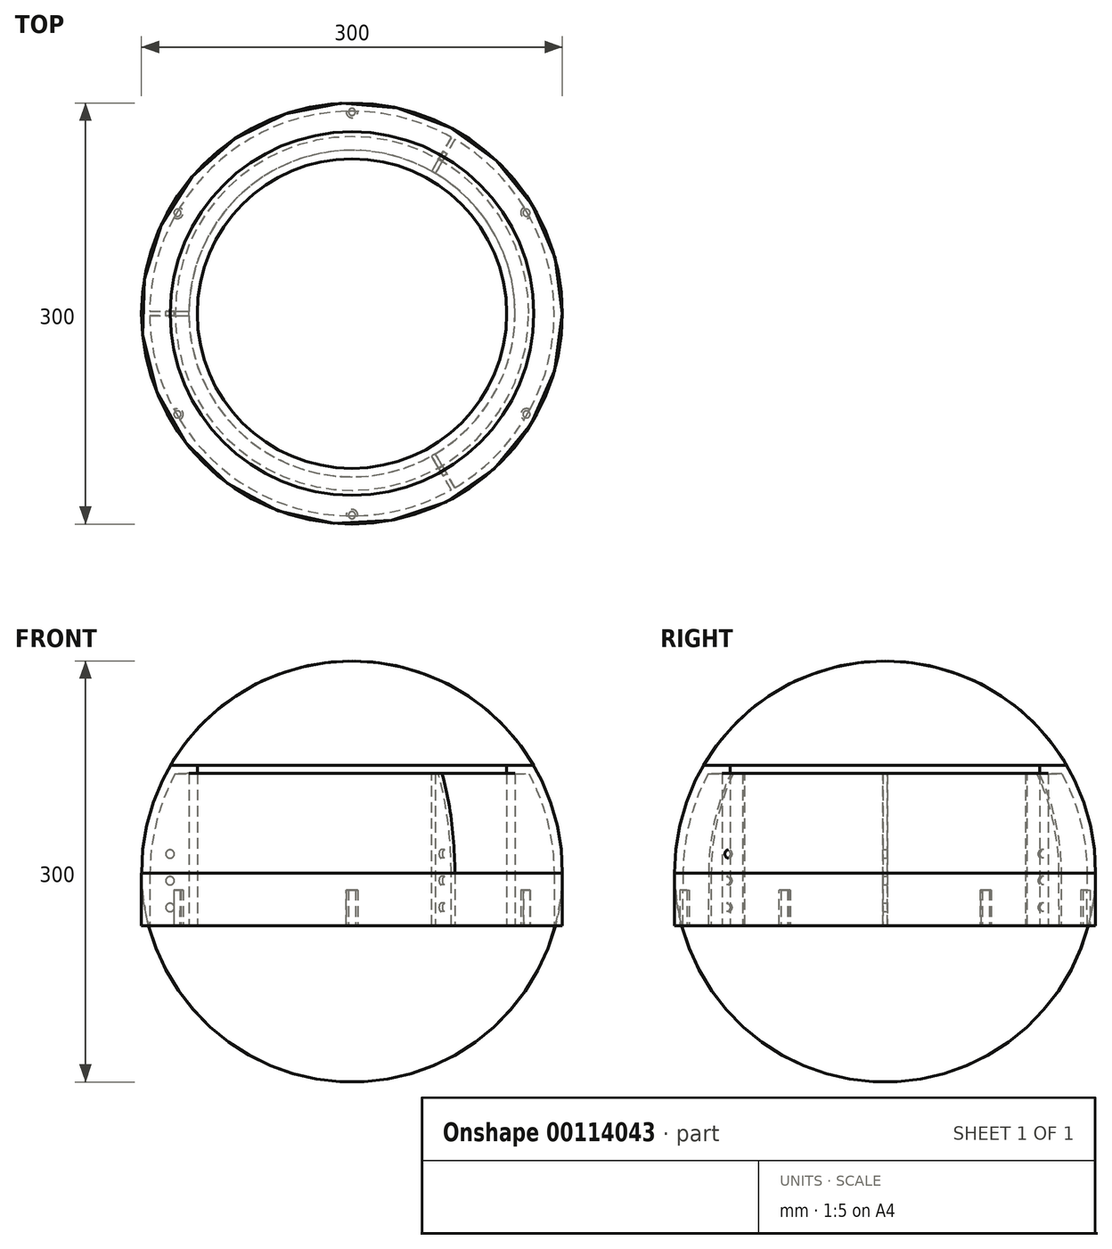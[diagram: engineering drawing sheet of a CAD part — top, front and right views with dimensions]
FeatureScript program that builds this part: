
annotation { "Feature Type Name" : "Feature", "Feature Type Description" : "" }
export const myFeature = defineFeature(function(context is Context, id is Id, definition is map)
    precondition{}
    {
        {
            var Q0;
            Q0=qCreatedBy(makeId("Front.planeOp"),FACE);
            var sketch = newSketch(context, id + "F0", { "sketchPlane" : qUnion([Q0])});
            skArc(sketch, "E0.trimOffspring", {"start": v(-125.97, 71) * mm, "mid": v(-139.35, 36.6) * mm, "end": v(-144, 0) * mm});
            skLineSegment(sketch, "E1", {"start": v(-116.3, 71.03) * mm, "end": v(-116.3, -24.99) * mm});
            skLineSegment(sketch, "E2", {"start": v(-150, 0) * mm, "end": v(-150, -37.33) * mm});
            skLineSegment(sketch, "E3", {"start": v(-150, -37.33) * mm, "end": v(-116.3, -37.33) * mm});
            skLineSegment(sketch, "E4", {"start": v(-116.3, -37.33) * mm, "end": v(-116.3, -24.99) * mm});
            skLineSegment(sketch, "E5", {"start": v(-144, 0) * mm, "end": v(-144.14, -37.33) * mm});
            skArc(sketch, "E6.trimOffspring", {"start": v(-129.51, 76.97) * mm, "mid": v(-144.96, 39.87) * mm, "end": v(-150, 0) * mm});
            skLineSegment(sketch, "E7", {"start": v(-129.51, 76.97) * mm, "end": v(-116.3, 76.97) * mm});
            skLineSegment(sketch, "E8", {"start": v(-116.3, 71.03) * mm, "end": v(-125.97, 71) * mm});
            skLineSegment(sketch, "E9", {"start": v(-125.99, 70.97) * mm, "end": v(-116.3, 70.97) * mm});
            skLineSegment(sketch, "E10", {"start": v(-110.3, 70.97) * mm, "end": v(-110.3, -37.33) * mm});
            skLineSegment(sketch, "E11", {"start": v(-110.3, -37.33) * mm, "end": v(-116.3, -37.33) * mm});
            skLineSegment(sketch, "E12", {"start": v(-116.3, 76.97) * mm, "end": v(-110.3, 76.97) * mm});
            skLineSegment(sketch, "E13", {"start": v(-110.3, 76.97) * mm, "end": v(-110.3, 70.97) * mm});
            skLineSegment(sketch, "E14", {"start": v(0, -70.43) * mm, "end": v(0, 79.54) * mm, "construction": true});
            skSolve(sketch);
        }
        {
            var Q0;
            {var subQ6=sQuery(id+"F0.wireOp",EDGE,"E2");Q0=makeQuery(id+"F0.imprint","IMPRINT",FACE,{"disambiguationData":[TD([[makeQuery(id+"F0.imprint","IMPRINT",EDGE,{"derivedFrom":subQ6}),1.0]])]});}
            var Q1;
            Q1=sQuery(id+"F0.wireOp",EDGE,"E14");
            revolve(context, id + "F1", {"entities" : qUnion([Q0]), "axis" : qUnion([Q1]), "revolveType" : RevolveType.FULL});
        }
        {
            var Q0;
            Q0=makeQuery(id+"F1.opRevolve","SWEPT_FACE",FACE,{"disambiguationData":[OSD([sQuery(id+"F0.wireOp",EDGE,"E3")])]});
            var sketch = newSketch(context, id + "F2", { "sketchPlane" : qUnion([Q0])});
            skCircle(sketch, "E15", {"center": v(0, 143.67) * mm, "radius": 2.5 * mm});
            skCircle(sketch, "E16", {"center": v(0, 143.67) * mm, "radius": 4.13 * mm});
            skCircle(sketch, "E17.1.0", {"center": v(-124.42, 71.83) * mm, "radius": 2.5 * mm});
            skCircle(sketch, "E17.2.0", {"center": v(-124.42, -71.83) * mm, "radius": 2.5 * mm});
            skCircle(sketch, "E17.3.0", {"center": v(0, -143.67) * mm, "radius": 2.5 * mm});
            skCircle(sketch, "E17.4.0", {"center": v(124.42, -71.83) * mm, "radius": 2.5 * mm});
            skCircle(sketch, "E17.5.0", {"center": v(124.42, 71.83) * mm, "radius": 2.5 * mm});
            skPoint(sketch, "E17.center", {"position": v(0, 0) * mm});
            skCircle(sketch, "E18.1.0", {"center": v(-124.42, -71.83) * mm, "radius": 4.13 * mm});
            skCircle(sketch, "E18.2.0", {"center": v(124.42, -71.83) * mm, "radius": 4.13 * mm});
            skCircle(sketch, "E19.1.0", {"center": v(-124.42, 71.83) * mm, "radius": 4.13 * mm});
            skCircle(sketch, "E19.3.0", {"center": v(0, -143.67) * mm, "radius": 4.13 * mm});
            skCircle(sketch, "E19.5.0", {"center": v(124.42, 71.83) * mm, "radius": 4.13 * mm});
            skSolve(sketch);
        }
        {
            var Q0;
            {var subQ0=sQuery(id+"F2.wireOp",EDGE,"E17.4.0");var subQ1=makeQuery(id+"F1.opRevolve","SWEPT_EDGE",EDGE,{"disambiguationData":[OSD([sQuery(id+"F0.wireOp",EDGE,"E3"),sQuery(id+"F0.wireOp",EDGE,"E5")])]});var subQ2=makeQuery(id+"F2.imprint","INTERSECT",VERTEX,{"disambiguationData":[OD(0.0)],"derivedFrom":[subQ1,subQ0]});Q0=makeQuery(id+"F2.imprint","IMPRINT",FACE,{"disambiguationData":[TD([[makeQuery(id+"F2.imprint","IMPRINT",EDGE,{"disambiguationData":[TD([[subQ2,-1.0]])],"derivedFrom":subQ0}),1.0]])]});}
            var Q1;
            {var subQ0=sQuery(id+"F2.wireOp",EDGE,"E15");var subQ1=makeQuery(id+"F1.opRevolve","SWEPT_EDGE",EDGE,{"disambiguationData":[OSD([sQuery(id+"F0.wireOp",EDGE,"E3"),sQuery(id+"F0.wireOp",EDGE,"E5")])]});var subQ2=makeQuery(id+"F2.imprint","INTERSECT",VERTEX,{"disambiguationData":[OD(0.0)],"derivedFrom":[subQ1,subQ0]});Q1=makeQuery(id+"F2.imprint","IMPRINT",FACE,{"disambiguationData":[TD([[makeQuery(id+"F2.imprint","IMPRINT",EDGE,{"disambiguationData":[TD([[subQ2,1.0]])],"derivedFrom":subQ0}),-1.0]])]});}
            var Q2;
            {var subQ0=sQuery(id+"F2.wireOp",EDGE,"E15");var subQ1=makeQuery(id+"F1.opRevolve","SWEPT_EDGE",EDGE,{"disambiguationData":[OSD([sQuery(id+"F0.wireOp",EDGE,"E3"),sQuery(id+"F0.wireOp",EDGE,"E5")])]});var subQ2=makeQuery(id+"F2.imprint","INTERSECT",VERTEX,{"disambiguationData":[OD(0.0)],"derivedFrom":[subQ1,subQ0]});Q2=makeQuery(id+"F2.imprint","IMPRINT",FACE,{"disambiguationData":[TD([[makeQuery(id+"F2.imprint","IMPRINT",EDGE,{"disambiguationData":[TD([[subQ2,-1.0]])],"derivedFrom":subQ0}),-1.0]])]});}
            var Q3;
            {var subQ0=sQuery(id+"F2.wireOp",EDGE,"E17.1.0");var subQ1=makeQuery(id+"F1.opRevolve","SWEPT_EDGE",EDGE,{"disambiguationData":[OSD([sQuery(id+"F0.wireOp",EDGE,"E3"),sQuery(id+"F0.wireOp",EDGE,"E5")])]});var subQ2=makeQuery(id+"F2.imprint","INTERSECT",VERTEX,{"disambiguationData":[OD(0.0)],"derivedFrom":[subQ1,subQ0]});Q3=makeQuery(id+"F2.imprint","IMPRINT",FACE,{"disambiguationData":[TD([[makeQuery(id+"F2.imprint","IMPRINT",EDGE,{"disambiguationData":[TD([[subQ2,-1.0]])],"derivedFrom":subQ0}),-1.0]])]});}
            var Q4;
            {var subQ0=sQuery(id+"F2.wireOp",EDGE,"E17.1.0");var subQ1=makeQuery(id+"F1.opRevolve","SWEPT_EDGE",EDGE,{"disambiguationData":[OSD([sQuery(id+"F0.wireOp",EDGE,"E3"),sQuery(id+"F0.wireOp",EDGE,"E5")])]});var subQ2=makeQuery(id+"F2.imprint","INTERSECT",VERTEX,{"disambiguationData":[OD(0.0)],"derivedFrom":[subQ1,subQ0]});Q4=makeQuery(id+"F2.imprint","IMPRINT",FACE,{"disambiguationData":[TD([[makeQuery(id+"F2.imprint","IMPRINT",EDGE,{"disambiguationData":[TD([[subQ2,1.0]])],"derivedFrom":subQ0}),-1.0]])]});}
            var Q5;
            {var subQ0=sQuery(id+"F2.wireOp",EDGE,"E17.5.0");var subQ1=makeQuery(id+"F1.opRevolve","SWEPT_EDGE",EDGE,{"disambiguationData":[OSD([sQuery(id+"F0.wireOp",EDGE,"E3"),sQuery(id+"F0.wireOp",EDGE,"E5")])]});var subQ2=makeQuery(id+"F2.imprint","INTERSECT",VERTEX,{"disambiguationData":[OD(0.0)],"derivedFrom":[subQ1,subQ0]});Q5=makeQuery(id+"F2.imprint","IMPRINT",FACE,{"disambiguationData":[TD([[makeQuery(id+"F2.imprint","IMPRINT",EDGE,{"disambiguationData":[TD([[subQ2,-1.0]])],"derivedFrom":subQ0}),-1.0]])]});}
            var Q6;
            {var subQ0=sQuery(id+"F2.wireOp",EDGE,"E17.5.0");var subQ1=makeQuery(id+"F1.opRevolve","SWEPT_EDGE",EDGE,{"disambiguationData":[OSD([sQuery(id+"F0.wireOp",EDGE,"E3"),sQuery(id+"F0.wireOp",EDGE,"E5")])]});var subQ2=makeQuery(id+"F2.imprint","INTERSECT",VERTEX,{"disambiguationData":[OD(0.0)],"derivedFrom":[subQ1,subQ0]});Q6=makeQuery(id+"F2.imprint","IMPRINT",FACE,{"disambiguationData":[TD([[makeQuery(id+"F2.imprint","IMPRINT",EDGE,{"disambiguationData":[TD([[subQ2,1.0]])],"derivedFrom":subQ0}),-1.0]])]});}
            var Q7;
            {var subQ0=sQuery(id+"F2.wireOp",EDGE,"E17.2.0");var subQ1=makeQuery(id+"F1.opRevolve","SWEPT_EDGE",EDGE,{"disambiguationData":[OSD([sQuery(id+"F0.wireOp",EDGE,"E3"),sQuery(id+"F0.wireOp",EDGE,"E5")])]});var subQ2=makeQuery(id+"F2.imprint","INTERSECT",VERTEX,{"disambiguationData":[OD(0.0)],"derivedFrom":[subQ1,subQ0]});Q7=makeQuery(id+"F2.imprint","IMPRINT",FACE,{"disambiguationData":[TD([[makeQuery(id+"F2.imprint","IMPRINT",EDGE,{"disambiguationData":[TD([[subQ2,-1.0]])],"derivedFrom":subQ0}),-1.0]])]});}
            var Q8;
            {var subQ0=sQuery(id+"F2.wireOp",EDGE,"E17.2.0");var subQ1=makeQuery(id+"F1.opRevolve","SWEPT_EDGE",EDGE,{"disambiguationData":[OSD([sQuery(id+"F0.wireOp",EDGE,"E3"),sQuery(id+"F0.wireOp",EDGE,"E5")])]});var subQ2=makeQuery(id+"F2.imprint","INTERSECT",VERTEX,{"disambiguationData":[OD(0.0)],"derivedFrom":[subQ1,subQ0]});Q8=makeQuery(id+"F2.imprint","IMPRINT",FACE,{"disambiguationData":[TD([[makeQuery(id+"F2.imprint","IMPRINT",EDGE,{"disambiguationData":[TD([[subQ2,1.0]])],"derivedFrom":subQ0}),-1.0]])]});}
            var Q9;
            {var subQ0=sQuery(id+"F2.wireOp",EDGE,"E17.2.0");var subQ1=makeQuery(id+"F1.opRevolve","SWEPT_EDGE",EDGE,{"disambiguationData":[OSD([sQuery(id+"F0.wireOp",EDGE,"E3"),sQuery(id+"F0.wireOp",EDGE,"E5")])]});var subQ2=makeQuery(id+"F2.imprint","INTERSECT",VERTEX,{"disambiguationData":[OD(0.0)],"derivedFrom":[subQ1,subQ0]});Q9=makeQuery(id+"F2.imprint","IMPRINT",FACE,{"disambiguationData":[TD([[makeQuery(id+"F2.imprint","IMPRINT",EDGE,{"disambiguationData":[TD([[subQ2,-1.0]])],"derivedFrom":subQ0}),1.0]])]});}
            var Q10;
            {var subQ0=sQuery(id+"F2.wireOp",EDGE,"E17.4.0");var subQ1=makeQuery(id+"F1.opRevolve","SWEPT_EDGE",EDGE,{"disambiguationData":[OSD([sQuery(id+"F0.wireOp",EDGE,"E3"),sQuery(id+"F0.wireOp",EDGE,"E5")])]});var subQ2=makeQuery(id+"F2.imprint","INTERSECT",VERTEX,{"disambiguationData":[OD(0.0)],"derivedFrom":[subQ1,subQ0]});Q10=makeQuery(id+"F2.imprint","IMPRINT",FACE,{"disambiguationData":[TD([[makeQuery(id+"F2.imprint","IMPRINT",EDGE,{"disambiguationData":[TD([[subQ2,-1.0]])],"derivedFrom":subQ0}),-1.0]])]});}
            var Q11;
            {var subQ0=sQuery(id+"F2.wireOp",EDGE,"E17.4.0");var subQ1=makeQuery(id+"F1.opRevolve","SWEPT_EDGE",EDGE,{"disambiguationData":[OSD([sQuery(id+"F0.wireOp",EDGE,"E3"),sQuery(id+"F0.wireOp",EDGE,"E5")])]});var subQ2=makeQuery(id+"F2.imprint","INTERSECT",VERTEX,{"disambiguationData":[OD(0.0)],"derivedFrom":[subQ1,subQ0]});Q11=makeQuery(id+"F2.imprint","IMPRINT",FACE,{"disambiguationData":[TD([[makeQuery(id+"F2.imprint","IMPRINT",EDGE,{"disambiguationData":[TD([[subQ2,1.0]])],"derivedFrom":subQ0}),-1.0]])]});}
            var Q12;
            {var subQ0=sQuery(id+"F2.wireOp",EDGE,"E17.3.0");var subQ1=makeQuery(id+"F1.opRevolve","SWEPT_EDGE",EDGE,{"disambiguationData":[OSD([sQuery(id+"F0.wireOp",EDGE,"E3"),sQuery(id+"F0.wireOp",EDGE,"E5")])]});var subQ2=makeQuery(id+"F2.imprint","INTERSECT",VERTEX,{"disambiguationData":[OD(0.0)],"derivedFrom":[subQ1,subQ0]});Q12=makeQuery(id+"F2.imprint","IMPRINT",FACE,{"disambiguationData":[TD([[makeQuery(id+"F2.imprint","IMPRINT",EDGE,{"disambiguationData":[TD([[subQ2,1.0]])],"derivedFrom":subQ0}),-1.0]])]});}
            extrude(context, id + "F3", {"entities" : qUnion([Q0, Q1, Q2, Q3, Q4, Q5, Q6, Q7, Q8, Q9, Q10, Q11, Q12]), "operationType" : NewBodyOperationType.ADD, "oppositeDirection" : true, "depth" : 25.4 * mm});
        }
        {
            var Q0;
            {var subQ0=sQuery(id+"F2.wireOp",EDGE,"E17.1.0");var subQ1=makeQuery(id+"F1.opRevolve","SWEPT_EDGE",EDGE,{"disambiguationData":[OSD([sQuery(id+"F0.wireOp",EDGE,"E3"),sQuery(id+"F0.wireOp",EDGE,"E5")])]});var subQ2=makeQuery(id+"F2.imprint","INTERSECT",VERTEX,{"disambiguationData":[OD(0.0)],"derivedFrom":[subQ1,subQ0]});Q0=makeQuery(id+"F2.imprint","IMPRINT",FACE,{"disambiguationData":[TD([[makeQuery(id+"F2.imprint","IMPRINT",EDGE,{"disambiguationData":[TD([[subQ2,1.0]])],"derivedFrom":subQ0}),1.0]])]});}
            var Q1;
            {var subQ0=sQuery(id+"F2.wireOp",EDGE,"E17.1.0");var subQ1=makeQuery(id+"F1.opRevolve","SWEPT_EDGE",EDGE,{"disambiguationData":[OSD([sQuery(id+"F0.wireOp",EDGE,"E3"),sQuery(id+"F0.wireOp",EDGE,"E5")])]});var subQ2=makeQuery(id+"F2.imprint","INTERSECT",VERTEX,{"disambiguationData":[OD(0.0)],"derivedFrom":[subQ1,subQ0]});Q1=makeQuery(id+"F2.imprint","IMPRINT",FACE,{"disambiguationData":[TD([[makeQuery(id+"F2.imprint","IMPRINT",EDGE,{"disambiguationData":[TD([[subQ2,-1.0]])],"derivedFrom":subQ0}),1.0]])]});}
            var Q2;
            {var subQ0=sQuery(id+"F2.wireOp",EDGE,"E15");var subQ1=makeQuery(id+"F1.opRevolve","SWEPT_EDGE",EDGE,{"disambiguationData":[OSD([sQuery(id+"F0.wireOp",EDGE,"E3"),sQuery(id+"F0.wireOp",EDGE,"E5")])]});var subQ2=makeQuery(id+"F2.imprint","INTERSECT",VERTEX,{"disambiguationData":[OD(0.0)],"derivedFrom":[subQ1,subQ0]});Q2=makeQuery(id+"F2.imprint","IMPRINT",FACE,{"disambiguationData":[TD([[makeQuery(id+"F2.imprint","IMPRINT",EDGE,{"disambiguationData":[TD([[subQ2,1.0]])],"derivedFrom":subQ0}),1.0]])]});}
            var Q3;
            {var subQ0=sQuery(id+"F2.wireOp",EDGE,"E15");var subQ1=makeQuery(id+"F1.opRevolve","SWEPT_EDGE",EDGE,{"disambiguationData":[OSD([sQuery(id+"F0.wireOp",EDGE,"E3"),sQuery(id+"F0.wireOp",EDGE,"E5")])]});var subQ2=makeQuery(id+"F2.imprint","INTERSECT",VERTEX,{"disambiguationData":[OD(0.0)],"derivedFrom":[subQ1,subQ0]});Q3=makeQuery(id+"F2.imprint","IMPRINT",FACE,{"disambiguationData":[TD([[makeQuery(id+"F2.imprint","IMPRINT",EDGE,{"disambiguationData":[TD([[subQ2,-1.0]])],"derivedFrom":subQ0}),1.0]])]});}
            var Q4;
            {var subQ0=sQuery(id+"F2.wireOp",EDGE,"E17.5.0");var subQ1=makeQuery(id+"F1.opRevolve","SWEPT_EDGE",EDGE,{"disambiguationData":[OSD([sQuery(id+"F0.wireOp",EDGE,"E3"),sQuery(id+"F0.wireOp",EDGE,"E5")])]});var subQ2=makeQuery(id+"F2.imprint","INTERSECT",VERTEX,{"disambiguationData":[OD(0.0)],"derivedFrom":[subQ1,subQ0]});Q4=makeQuery(id+"F2.imprint","IMPRINT",FACE,{"disambiguationData":[TD([[makeQuery(id+"F2.imprint","IMPRINT",EDGE,{"disambiguationData":[TD([[subQ2,1.0]])],"derivedFrom":subQ0}),1.0]])]});}
            var Q5;
            {var subQ0=sQuery(id+"F2.wireOp",EDGE,"E17.5.0");var subQ1=makeQuery(id+"F1.opRevolve","SWEPT_EDGE",EDGE,{"disambiguationData":[OSD([sQuery(id+"F0.wireOp",EDGE,"E3"),sQuery(id+"F0.wireOp",EDGE,"E5")])]});var subQ2=makeQuery(id+"F2.imprint","INTERSECT",VERTEX,{"disambiguationData":[OD(0.0)],"derivedFrom":[subQ1,subQ0]});Q5=makeQuery(id+"F2.imprint","IMPRINT",FACE,{"disambiguationData":[TD([[makeQuery(id+"F2.imprint","IMPRINT",EDGE,{"disambiguationData":[TD([[subQ2,-1.0]])],"derivedFrom":subQ0}),1.0]])]});}
            var Q6;
            {var subQ0=sQuery(id+"F2.wireOp",EDGE,"E17.2.0");var subQ1=makeQuery(id+"F1.opRevolve","SWEPT_EDGE",EDGE,{"disambiguationData":[OSD([sQuery(id+"F0.wireOp",EDGE,"E3"),sQuery(id+"F0.wireOp",EDGE,"E5")])]});var subQ2=makeQuery(id+"F2.imprint","INTERSECT",VERTEX,{"disambiguationData":[OD(0.0)],"derivedFrom":[subQ1,subQ0]});Q6=makeQuery(id+"F2.imprint","IMPRINT",FACE,{"disambiguationData":[TD([[makeQuery(id+"F2.imprint","IMPRINT",EDGE,{"disambiguationData":[TD([[subQ2,-1.0]])],"derivedFrom":subQ0}),1.0]])]});}
            var Q7;
            {var subQ0=sQuery(id+"F2.wireOp",EDGE,"E17.2.0");var subQ1=makeQuery(id+"F1.opRevolve","SWEPT_EDGE",EDGE,{"disambiguationData":[OSD([sQuery(id+"F0.wireOp",EDGE,"E3"),sQuery(id+"F0.wireOp",EDGE,"E5")])]});var subQ2=makeQuery(id+"F2.imprint","INTERSECT",VERTEX,{"disambiguationData":[OD(0.0)],"derivedFrom":[subQ1,subQ0]});Q7=makeQuery(id+"F2.imprint","IMPRINT",FACE,{"disambiguationData":[TD([[makeQuery(id+"F2.imprint","IMPRINT",EDGE,{"disambiguationData":[TD([[subQ2,1.0]])],"derivedFrom":subQ0}),1.0]])]});}
            var Q8;
            {var subQ0=sQuery(id+"F2.wireOp",EDGE,"E17.3.0");var subQ1=makeQuery(id+"F1.opRevolve","SWEPT_EDGE",EDGE,{"disambiguationData":[OSD([sQuery(id+"F0.wireOp",EDGE,"E3"),sQuery(id+"F0.wireOp",EDGE,"E5")])]});var subQ2=makeQuery(id+"F2.imprint","INTERSECT",VERTEX,{"disambiguationData":[OD(0.0)],"derivedFrom":[subQ1,subQ0]});Q8=makeQuery(id+"F2.imprint","IMPRINT",FACE,{"disambiguationData":[TD([[makeQuery(id+"F2.imprint","IMPRINT",EDGE,{"disambiguationData":[TD([[subQ2,-1.0]])],"derivedFrom":subQ0}),1.0]])]});}
            var Q9;
            {var subQ0=sQuery(id+"F2.wireOp",EDGE,"E17.3.0");var subQ1=makeQuery(id+"F1.opRevolve","SWEPT_EDGE",EDGE,{"disambiguationData":[OSD([sQuery(id+"F0.wireOp",EDGE,"E3"),sQuery(id+"F0.wireOp",EDGE,"E5")])]});var subQ2=makeQuery(id+"F2.imprint","INTERSECT",VERTEX,{"disambiguationData":[OD(0.0)],"derivedFrom":[subQ1,subQ0]});Q9=makeQuery(id+"F2.imprint","IMPRINT",FACE,{"disambiguationData":[TD([[makeQuery(id+"F2.imprint","IMPRINT",EDGE,{"disambiguationData":[TD([[subQ2,1.0]])],"derivedFrom":subQ0}),1.0]])]});}
            var Q10;
            {var subQ0=sQuery(id+"F2.wireOp",EDGE,"E17.4.0");var subQ1=makeQuery(id+"F1.opRevolve","SWEPT_EDGE",EDGE,{"disambiguationData":[OSD([sQuery(id+"F0.wireOp",EDGE,"E3"),sQuery(id+"F0.wireOp",EDGE,"E5")])]});var subQ2=makeQuery(id+"F2.imprint","INTERSECT",VERTEX,{"disambiguationData":[OD(0.0)],"derivedFrom":[subQ1,subQ0]});Q10=makeQuery(id+"F2.imprint","IMPRINT",FACE,{"disambiguationData":[TD([[makeQuery(id+"F2.imprint","IMPRINT",EDGE,{"disambiguationData":[TD([[subQ2,-1.0]])],"derivedFrom":subQ0}),1.0]])]});}
            var Q11;
            {var subQ0=sQuery(id+"F2.wireOp",EDGE,"E17.4.0");var subQ1=makeQuery(id+"F1.opRevolve","SWEPT_EDGE",EDGE,{"disambiguationData":[OSD([sQuery(id+"F0.wireOp",EDGE,"E3"),sQuery(id+"F0.wireOp",EDGE,"E5")])]});var subQ2=makeQuery(id+"F2.imprint","INTERSECT",VERTEX,{"disambiguationData":[OD(0.0)],"derivedFrom":[subQ1,subQ0]});Q11=makeQuery(id+"F2.imprint","IMPRINT",FACE,{"disambiguationData":[TD([[makeQuery(id+"F2.imprint","IMPRINT",EDGE,{"disambiguationData":[TD([[subQ2,1.0]])],"derivedFrom":subQ0}),1.0]])]});}
            extrude(context, id + "F4", {"entities" : qUnion([Q0, Q1, Q2, Q3, Q4, Q5, Q6, Q7, Q8, Q9, Q10, Q11]), "operationType" : NewBodyOperationType.REMOVE, "oppositeDirection" : true, "depth" : 25.4 * mm});
        }
        {
            var Q0;
            {var subQ0=sQuery(id+"F0.wireOp",EDGE,"E4");Q0=makeQuery(id+"F0.imprint","IMPRINT",FACE,{"disambiguationData":[TD([[makeQuery(id+"F0.imprint","IMPRINT",EDGE,{"derivedFrom":subQ0}),1.0]])]});}
            extrude(context, id + "F5", {"entities" : qUnion([Q0]), "operationType" : NewBodyOperationType.ADD, "endBound" : BoundingType.SYMMETRIC, "depth" : 3 * mm});
        }
        {
            var Q0;
            Q0=makeQuery(id+"F5.opExtrude","CAP_FACE",FACE,{"disambiguationData":[OSD([sQuery(id+"F0.wireOp",EDGE,"E0.trimOffspring"),sQuery(id+"F0.wireOp",EDGE,"E1"),sQuery(id+"F0.wireOp",EDGE,"E3"),sQuery(id+"F0.wireOp",EDGE,"E4"),sQuery(id+"F0.wireOp",EDGE,"E5"),sQuery(id+"F0.wireOp",EDGE,"E9")])],"isStart":true});
            var sketch = newSketch(context, id + "F6", { "sketchPlane" : qUnion([Q0])});
            skCircle(sketch, "E20", {"center": v(129.7, 13.75) * mm, "radius": 3 * mm});
            skCircle(sketch, "E21", {"center": v(129.7, -5.3) * mm, "radius": 3 * mm});
            skCircle(sketch, "E22", {"center": v(129.7, -24.35) * mm, "radius": 3 * mm});
            skSolve(sketch);
        }
        {
            var Q0;
            Q0 = qSketchRegion(id + "F6", true);
            extrude(context, id + "F7", {"entities" : qUnion([Q0]), "operationType" : NewBodyOperationType.REMOVE, "oppositeDirection" : true, "depth" : 25.4 * mm});
        }
        {
            var Q0;
            Q0=makeQuery(id+"F1.opRevolve","SWEPT_BODY",BODY,{"disambiguationData":[OSD([sQuery(id+"F0.wireOp",EDGE,"E0.trimOffspring"),sQuery(id+"F0.wireOp",EDGE,"E1"),sQuery(id+"F0.wireOp",EDGE,"E2"),sQuery(id+"F0.wireOp",EDGE,"E3"),sQuery(id+"F0.wireOp",EDGE,"E4"),sQuery(id+"F0.wireOp",EDGE,"E5"),sQuery(id+"F0.wireOp",EDGE,"E6.trimOffspring"),sQuery(id+"F0.wireOp",EDGE,"E7"),sQuery(id+"F0.wireOp",EDGE,"E8"),sQuery(id+"F0.wireOp",EDGE,"E10"),sQuery(id+"F0.wireOp",EDGE,"E11"),sQuery(id+"F0.wireOp",EDGE,"E12"),sQuery(id+"F0.wireOp",EDGE,"E13")])]});
            var Q1;
            Q1=sQuery(id+"F0.wireOp",EDGE,"E14");
            circularPattern(context, id + "F8", {"operationType" : NewBodyOperationType.ADD, "entities" : qUnion([Q0]), "axis" : qUnion([Q1]), "angle" : 360 * degree, "instanceCount" : 3, "equalSpace" : true});
        }
    });
